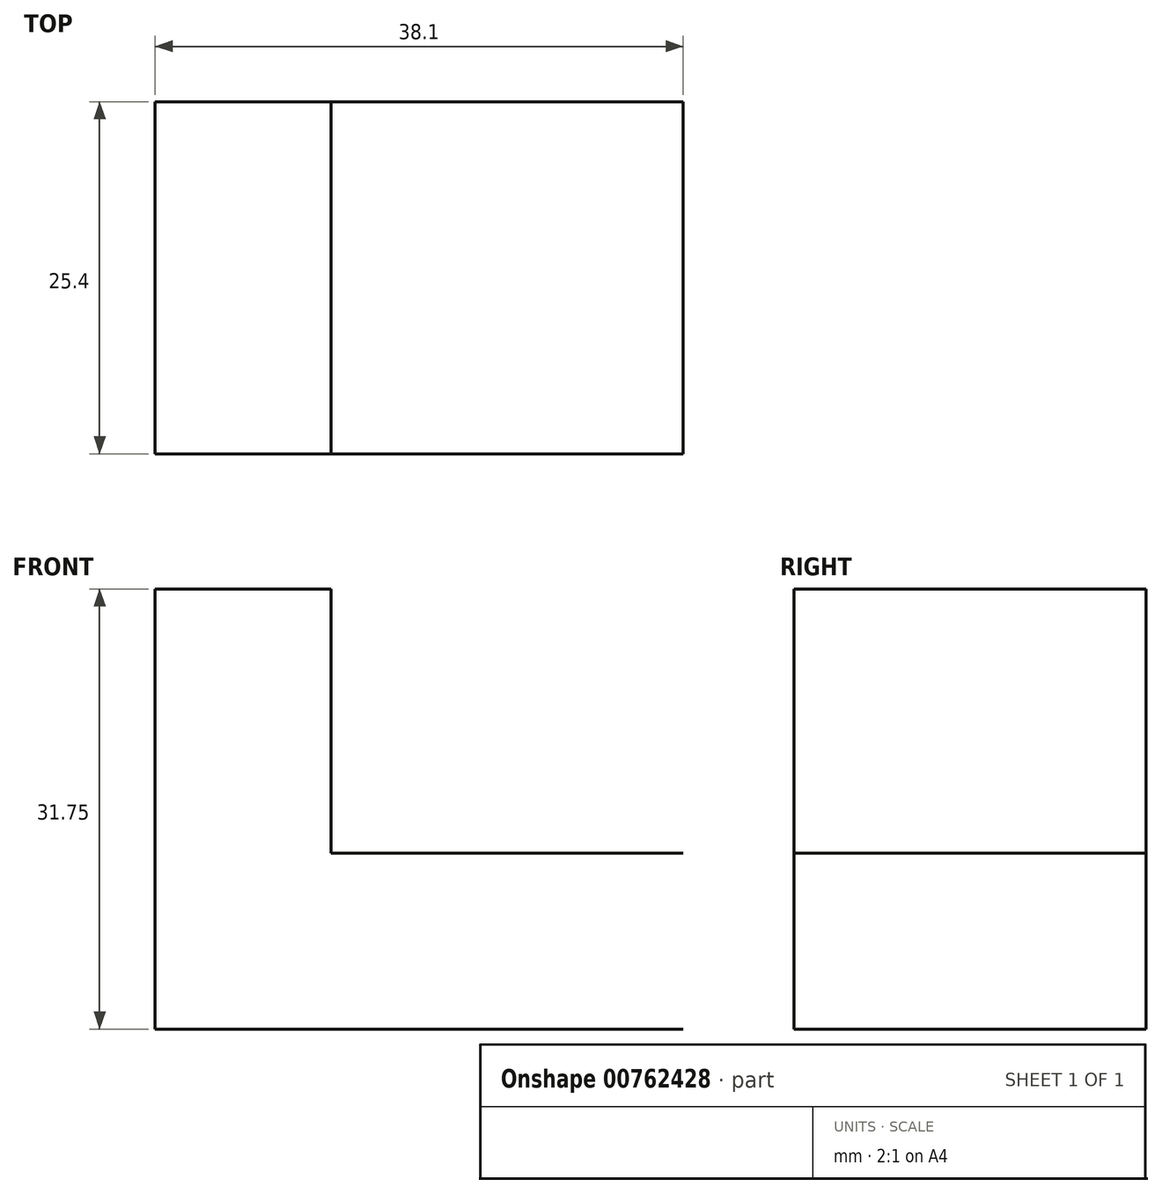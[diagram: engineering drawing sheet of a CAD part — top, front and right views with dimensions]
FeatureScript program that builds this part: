
annotation { "Feature Type Name" : "Feature", "Feature Type Description" : "" }
export const myFeature = defineFeature(function(context is Context, id is Id, definition is map)
    precondition{}
    {
        {
            var Q0;
            Q0=qCreatedBy(makeId("Front.planeOp"),FACE);
            var sketch = newSketch(context, id + "F0", { "sketchPlane" : qUnion([Q0])});
            skLineSegment(sketch, "E0", {"start": v(0, 0) * mm, "end": v(38.1, 0) * mm});
            skLineSegment(sketch, "E1", {"start": v(38.1, 0) * mm, "end": v(38.1, 12.7) * mm});
            skLineSegment(sketch, "E2", {"start": v(38.1, 12.7) * mm, "end": v(12.7, 12.7) * mm});
            skLineSegment(sketch, "E3", {"start": v(12.7, 12.7) * mm, "end": v(12.7, 31.75) * mm});
            skLineSegment(sketch, "E4", {"start": v(0, 0) * mm, "end": v(0, 31.75) * mm});
            skLineSegment(sketch, "E5", {"start": v(0, 31.75) * mm, "end": v(12.7, 31.75) * mm});
            skSolve(sketch);
        }
        {
            var Q0;
            Q0=sQuery(id+"F0.wireOp",EDGE,"E0");
            var Q1;
            Q1=sQuery(id+"F0.wireOp",EDGE,"E2");
            var Q2;
            Q2=sQuery(id+"F0.wireOp",EDGE,"E5");
            var Q3;
            Q3=sQuery(id+"F0.wireOp",EDGE,"E4");
            var Q4;
            Q4=sQuery(id+"F0.wireOp",EDGE,"E3");
            extrude(context, id + "F1", {"bodyType" : ToolBodyType.SURFACE, "surfaceEntities" : qUnion([Q0, Q1, Q2, Q3, Q4]), "depth" : 25.4 * mm, "offsetDistance" : 25.4 * mm});
        }
    });
